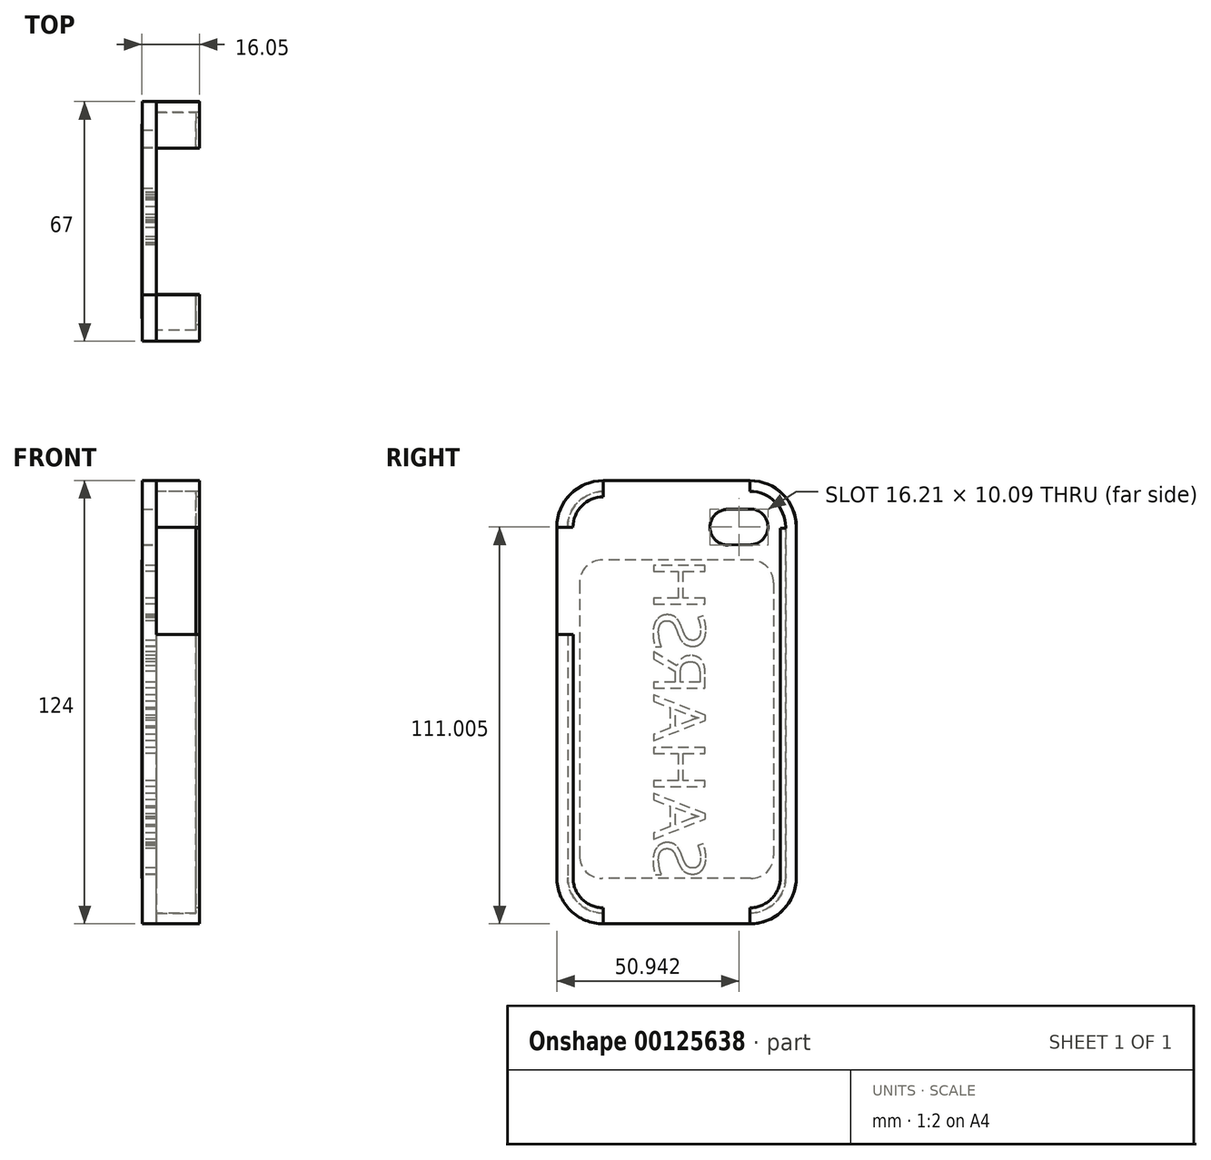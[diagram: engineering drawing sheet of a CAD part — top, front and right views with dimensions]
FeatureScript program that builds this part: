
annotation { "Feature Type Name" : "Feature", "Feature Type Description" : "" }
export const myFeature = defineFeature(function(context is Context, id is Id, definition is map)
    precondition{}
    {
        {
            var Q0;
            Q0=qCreatedBy(makeId("Right.planeOp"),FACE);
            var sketch = newSketch(context, id + "F0", { "sketchPlane" : qUnion([Q0])});
            skLineSegment(sketch, "E0.rect.bottom", {"start": v(20.5, 62) * mm, "end": v(-20.5, 62) * mm});
            skLineSegment(sketch, "E0.rect.top", {"start": v(20.5, -62) * mm, "end": v(-20.5, -62) * mm});
            skLineSegment(sketch, "E0.rect.left", {"start": v(33.5, 49) * mm, "end": v(33.5, -49) * mm});
            skLineSegment(sketch, "E0.rect.right", {"start": v(-33.5, 49) * mm, "end": v(-33.5, -49) * mm});
            skPoint(sketch, "E0.rect.middle", {"position": v(0, 0) * mm});
            skPoint(sketch, "E1.visualSharp", {"position": v(-33.5, 62) * mm});
            skArc(sketch, "E1.filletArc", {"start": v(-20.5, 62) * mm, "mid": v(-29.7, 58.2) * mm, "end": v(-33.5, 49) * mm});
            skPoint(sketch, "E2.visualSharp", {"position": v(-33.5, -62) * mm});
            skArc(sketch, "E2.filletArc", {"start": v(-33.5, -49) * mm, "mid": v(-29.7, -58.2) * mm, "end": v(-20.5, -62) * mm});
            skPoint(sketch, "E3.visualSharp", {"position": v(33.5, 62) * mm});
            skArc(sketch, "E3.filletArc", {"start": v(33.5, 49) * mm, "mid": v(29.7, 58.2) * mm, "end": v(20.5, 62) * mm});
            skPoint(sketch, "E4.visualSharp", {"position": v(33.5, -62) * mm});
            skArc(sketch, "E4.filletArc", {"start": v(20.5, -62) * mm, "mid": v(29.7, -58.2) * mm, "end": v(33.5, -49) * mm});
            skSolve(sketch);
        }
        {
            var Q0;
            Q0=qSketchRegion(id+"F0",true);
            extrude(context, id + "F1", {"entities" : qUnion([Q0]), "depth" : 4 * mm});
        }
        {
            var Q0;
            Q0=qCreatedBy(makeId("Right.planeOp"),FACE);
            var sketch = newSketch(context, id + "F2", { "sketchPlane" : qUnion([Q0])});
            skArc(sketch, "E5", {"start": v(20.7, 44.05) * mm, "mid": v(25.55, 49.12) * mm, "end": v(20.55, 54.05) * mm});
            skLineSegment(sketch, "E6", {"start": v(20.55, 54.05) * mm, "end": v(14.26, 53.96) * mm});
            skLineSegment(sketch, "E7", {"start": v(20.7, 44.05) * mm, "end": v(14.4, 43.96) * mm});
            skArc(sketch, "E8", {"start": v(14.26, 53.96) * mm, "mid": v(9.34, 48.89) * mm, "end": v(14.4, 43.96) * mm});
            skLineSegment(sketch, "E9", {"start": v(14.26, 53.96) * mm, "end": v(14.4, 43.96) * mm, "construction": true});
            skLineSegment(sketch, "E10", {"start": v(20.55, 54.05) * mm, "end": v(20.7, 44.05) * mm, "construction": true});
            skSolve(sketch);
        }
        {
            var Q0;
            Q0=makeQuery(id+"F2.imprint","IMPRINT",FACE,{"disambiguationData":[TD([[makeQuery(id+"F2.imprint","IMPRINT",EDGE,{"derivedFrom":sQuery(id+"F2.wireOp",EDGE,"E5")}),1.0]])]});
            extrude(context, id + "F3", {"entities" : qUnion([Q0]), "operationType" : NewBodyOperationType.REMOVE, "oppositeDirection" : true, "depth" : 25.4 * mm, "hasSecondDirection" : true, "secondDirectionOppositeDirection" : false, "secondDirectionDepth" : 33.72 * mm});
        }
        {
            var Q0;
            Q0=qCreatedBy(makeId("Right.planeOp"),FACE);
            var sketch = newSketch(context, id + "F4", { "sketchPlane" : qUnion([Q0])});
            skLineSegment(sketch, "E11", {"start": v(-30.46, 18.92) * mm, "end": v(-33.5, 18.92) * mm});
            skLineSegment(sketch, "E12", {"start": v(-33.5, 18.92) * mm, "end": v(-33.5, -49) * mm});
            skLineSegment(sketch, "E13", {"start": v(-33.5, -49) * mm, "end": v(-30.46, -49) * mm});
            skLineSegment(sketch, "E14", {"start": v(-30.46, -49) * mm, "end": v(-30.46, 18.92) * mm});
            skSolve(sketch);
        }
        {
            var Q0;
            Q0=qSketchRegion(id+"F4",true);
            extrude(context, id + "F5", {"entities" : qUnion([Q0]), "operationType" : NewBodyOperationType.ADD, "depth" : 16 * mm});
        }
        {
            var Q0;
            Q0=qCreatedBy(makeId("Right.planeOp"),FACE);
            var sketch = newSketch(context, id + "F6", { "sketchPlane" : qUnion([Q0])});
            skLineSegment(sketch, "E15", {"start": v(-33.5, -49) * mm, "end": v(-30.46, -49) * mm});
            skLineSegment(sketch, "E16", {"start": v(-20.5, -59) * mm, "end": v(-20.5, -62) * mm});
            skArc(sketch, "E17", {"start": v(-30.46, -49) * mm, "mid": v(-27.56, -56.07) * mm, "end": v(-20.5, -59) * mm});
            skArc(sketch, "E18", {"start": v(-33.5, -49) * mm, "mid": v(-29.7, -58.2) * mm, "end": v(-20.5, -62) * mm});
            skSolve(sketch);
        }
        {
            var Q0;
            Q0=qSketchRegion(id+"F6",true);
            extrude(context, id + "F7", {"entities" : qUnion([Q0]), "operationType" : NewBodyOperationType.ADD, "depth" : 16 * mm});
        }
        {
            var Q0;
            Q0=qCreatedBy(makeId("Right.planeOp"),FACE);
            var sketch = newSketch(context, id + "F8", { "sketchPlane" : qUnion([Q0])});
            skLineSegment(sketch, "E19", {"start": v(-30.47, 48.93) * mm, "end": v(-33.5, 48.93) * mm});
            skLineSegment(sketch, "E20", {"start": v(-20.5, 62) * mm, "end": v(-20.5, 58.97) * mm});
            skArc(sketch, "E21", {"start": v(-20.5, 58.97) * mm, "mid": v(-27.55, 56) * mm, "end": v(-30.47, 48.93) * mm});
            skArc(sketch, "E22", {"start": v(-20.5, 62) * mm, "mid": v(-29.7, 58.15) * mm, "end": v(-33.5, 48.93) * mm});
            skSolve(sketch);
        }
        {
            var Q0;
            Q0=qSketchRegion(id+"F8",true);
            extrude(context, id + "F9", {"entities" : qUnion([Q0]), "operationType" : NewBodyOperationType.ADD, "depth" : 16 * mm});
        }
        {
            var Q0;
            Q0=qCreatedBy(makeId("Right.planeOp"),FACE);
            var sketch = newSketch(context, id + "F10", { "sketchPlane" : qUnion([Q0])});
            skLineSegment(sketch, "E23", {"start": v(20.49, -62) * mm, "end": v(20.49, -59) * mm});
            skLineSegment(sketch, "E24", {"start": v(33.5, -49) * mm, "end": v(30.5, -49) * mm});
            skArc(sketch, "E25", {"start": v(20.49, -59) * mm, "mid": v(27.55, -56.06) * mm, "end": v(30.5, -49) * mm});
            skArc(sketch, "E26", {"start": v(20.49, -62) * mm, "mid": v(29.67, -58.19) * mm, "end": v(33.5, -49) * mm});
            skSolve(sketch);
        }
        {
            var Q0;
            Q0=qSketchRegion(id+"F10",true);
            extrude(context, id + "F11", {"entities" : qUnion([Q0]), "operationType" : NewBodyOperationType.ADD, "depth" : 16 * mm});
        }
        {
            var Q0;
            Q0=qCreatedBy(makeId("Right.planeOp"),FACE);
            var sketch = newSketch(context, id + "F12", { "sketchPlane" : qUnion([Q0])});
            skLineSegment(sketch, "E27", {"start": v(33.46, 49) * mm, "end": v(30.5, 49) * mm});
            skLineSegment(sketch, "E28", {"start": v(20.5, 62) * mm, "end": v(20.5, 58.99) * mm});
            skArc(sketch, "E29", {"start": v(33.46, 49) * mm, "mid": v(29.66, 58.17) * mm, "end": v(20.5, 62) * mm});
            skArc(sketch, "E30", {"start": v(30.5, 49) * mm, "mid": v(27.55, 56.05) * mm, "end": v(20.5, 58.99) * mm});
            skSolve(sketch);
        }
        {
            var Q0;
            Q0=qSketchRegion(id+"F12",true);
            extrude(context, id + "F13", {"entities" : qUnion([Q0]), "operationType" : NewBodyOperationType.ADD, "depth" : 16 * mm});
        }
        {
            var Q0;
            Q0=qCreatedBy(makeId("Right.planeOp"),FACE);
            var sketch = newSketch(context, id + "F14", { "sketchPlane" : qUnion([Q0])});
            skLineSegment(sketch, "E31", {"start": v(30.5, -49) * mm, "end": v(33.49, -49) * mm});
            skLineSegment(sketch, "E32", {"start": v(33.49, -49) * mm, "end": v(33.49, 49) * mm});
            skLineSegment(sketch, "E33", {"start": v(33.49, 49) * mm, "end": v(30.5, 49) * mm});
            skLineSegment(sketch, "E34", {"start": v(30.5, 49) * mm, "end": v(30.5, -49) * mm});
            skSolve(sketch);
        }
        {
            var Q0;
            Q0=qSketchRegion(id+"F14",true);
            extrude(context, id + "F15", {"entities" : qUnion([Q0]), "operationType" : NewBodyOperationType.ADD, "depth" : 16 * mm});
        }
        {
            var Q0;
            Q0=qCreatedBy(makeId("Right.planeOp"),FACE);
            var sketch = newSketch(context, id + "F16", { "sketchPlane" : qUnion([Q0])});
            skLineSegment(sketch, "E35", {"start": v(-30.46, 18.92) * mm, "end": v(-30.46, -49.07) * mm});
            skLineSegment(sketch, "E36", {"start": v(-30.46, -49.07) * mm, "end": v(-28.96, -49.07) * mm});
            skLineSegment(sketch, "E37", {"start": v(-28.96, -49.07) * mm, "end": v(-28.96, 18.92) * mm});
            skLineSegment(sketch, "E38", {"start": v(-28.96, 18.92) * mm, "end": v(-30.46, 18.92) * mm});
            skLineSegment(sketch, "E39", {"start": v(-20.5, -59) * mm, "end": v(-20.5, -57.5) * mm});
            skArc(sketch, "E40", {"start": v(-30.46, -49.07) * mm, "mid": v(-27.53, -56.1) * mm, "end": v(-20.5, -59) * mm});
            skArc(sketch, "E41", {"start": v(-28.96, -49.07) * mm, "mid": v(-26.47, -55.04) * mm, "end": v(-20.5, -57.5) * mm});
            skLineSegment(sketch, "E42", {"start": v(-30.47, 48.93) * mm, "end": v(-28.97, 48.93) * mm});
            skLineSegment(sketch, "E43", {"start": v(-20.5, 58.97) * mm, "end": v(-20.5, 57.47) * mm});
            skArc(sketch, "E44", {"start": v(-20.5, 58.97) * mm, "mid": v(-27.55, 56) * mm, "end": v(-30.47, 48.93) * mm});
            skArc(sketch, "E45", {"start": v(-20.5, 57.47) * mm, "mid": v(-26.5, 54.95) * mm, "end": v(-28.97, 48.93) * mm});
            skLineSegment(sketch, "E46", {"start": v(30.5, 48.62) * mm, "end": v(29, 48.62) * mm});
            skLineSegment(sketch, "E47", {"start": v(30.5, -49) * mm, "end": v(29, -49) * mm});
            skLineSegment(sketch, "E48", {"start": v(29, -49) * mm, "end": v(29, 48.62) * mm});
            skLineSegment(sketch, "E49", {"start": v(30.5, 48.62) * mm, "end": v(30.5, -49) * mm});
            skLineSegment(sketch, "E50", {"start": v(20.49, -59) * mm, "end": v(20.49, -57.5) * mm});
            skArc(sketch, "E51", {"start": v(20.49, -59) * mm, "mid": v(27.54, -56.06) * mm, "end": v(30.5, -49) * mm});
            skArc(sketch, "E52", {"start": v(20.49, -57.5) * mm, "mid": v(26.5, -55.02) * mm, "end": v(29, -49) * mm});
            skSolve(sketch);
        }
        {
            var Q0;
            Q0=qSketchRegion(id+"F16",true);
            extrude(context, id + "F17", {"entities" : qUnion([Q0]), "operationType" : NewBodyOperationType.ADD, "depth" : 16 * mm, "hasSecondDirection" : true, "secondDirectionOppositeDirection" : false, "secondDirectionDepth" : 15 * mm});
        }
        {
            var Q0;
            Q0=makeQuery(id+"F7.boolean.opBoolean","MERGE",FACE,{"derivedFrom":[makeQuery(id+"F1.opExtrude","CAP_FACE",FACE,{"disambiguationData":[OSD([sQuery(id+"F0.wireOp",EDGE,"E0.rect.bottom"),sQuery(id+"F0.wireOp",EDGE,"E0.rect.top"),sQuery(id+"F0.wireOp",EDGE,"E0.rect.left"),sQuery(id+"F0.wireOp",EDGE,"E0.rect.right"),sQuery(id+"F0.wireOp",EDGE,"E1.filletArc"),sQuery(id+"F0.wireOp",EDGE,"E2.filletArc"),sQuery(id+"F0.wireOp",EDGE,"E3.filletArc"),sQuery(id+"F0.wireOp",EDGE,"E4.filletArc")])],"isStart":true}),makeQuery(id+"F7.opExtrude","CAP_FACE",FACE,{"disambiguationData":[OSD([sQuery(id+"F6.wireOp",EDGE,"E15"),sQuery(id+"F6.wireOp",EDGE,"E16"),sQuery(id+"F6.wireOp",EDGE,"E17"),sQuery(id+"F6.wireOp",EDGE,"E18")])],"isStart":true})]});
            var sketch = newSketch(context, id + "F18", { "sketchPlane" : qUnion([Q0])});
            skLineSegment(sketch, "E53.bottom", {"start": v(-20.8, 39.78) * mm, "end": v(20.8, 39.78) * mm});
            skLineSegment(sketch, "E53.top", {"start": v(-20.8, -49.3) * mm, "end": v(20.8, -49.3) * mm});
            skLineSegment(sketch, "E53.left", {"start": v(-27.15, 33.43) * mm, "end": v(-27.15, -42.95) * mm});
            skLineSegment(sketch, "E53.right", {"start": v(27.15, 33.42) * mm, "end": v(27.15, -42.95) * mm});
            skPoint(sketch, "E54.visualSharp", {"position": v(-27.15, 39.78) * mm});
            skArc(sketch, "E54.filletArc", {"start": v(-20.8, 39.78) * mm, "mid": v(-25.3, 37.92) * mm, "end": v(-27.15, 33.43) * mm});
            skPoint(sketch, "E55.visualSharp", {"position": v(-27.15, -49.3) * mm});
            skArc(sketch, "E55.filletArc", {"start": v(-27.15, -42.95) * mm, "mid": v(-25.3, -47.44) * mm, "end": v(-20.8, -49.3) * mm});
            skPoint(sketch, "E56.visualSharp", {"position": v(27.15, -49.3) * mm});
            skArc(sketch, "E56.filletArc", {"start": v(20.8, -49.3) * mm, "mid": v(25.3, -47.44) * mm, "end": v(27.15, -42.95) * mm});
            skPoint(sketch, "E57.visualSharp", {"position": v(27.15, 39.78) * mm});
            skArc(sketch, "E57.filletArc", {"start": v(27.15, 33.42) * mm, "mid": v(25.3, 37.92) * mm, "end": v(20.8, 39.78) * mm});
            skSolve(sketch);
        }
        {
            var Q0;
            Q0 = qSketchRegion(id + "F18", true);
            extrude(context, id + "F19", {"entities" : qUnion([Q0]), "operationType" : NewBodyOperationType.ADD, "depth" : 0.05 * mm});
        }
        {
            var Q0;
            Q0=makeQuery(id+"F19.opExtrude","CAP_FACE",FACE,{"disambiguationData":[OSD([sQuery(id+"F18.wireOp",EDGE,"E53.bottom"),sQuery(id+"F18.wireOp",EDGE,"E53.top"),sQuery(id+"F18.wireOp",EDGE,"E53.left"),sQuery(id+"F18.wireOp",EDGE,"E53.right"),sQuery(id+"F18.wireOp",EDGE,"E54.filletArc"),sQuery(id+"F18.wireOp",EDGE,"E55.filletArc"),sQuery(id+"F18.wireOp",EDGE,"E56.filletArc"),sQuery(id+"F18.wireOp",EDGE,"E57.filletArc")])],"isStart":false});
            var sketch = newSketch(context, id + "F20", { "sketchPlane" : qUnion([Q0])});
            skText(sketch, "E58", { "text": "SAHARSH", "fontName": "OpenSans-Regular.ttf"});
            const initialGuessF20  = {"E58": [0.00637, -0.0493, 0, 1, 0.01447]};
            skSetInitialGuess(sketch, initialGuessF20);
            skSolve(sketch);
        }
        {
            var Q0;
            Q0 = qSketchRegion(id + "F20", true);
            extrude(context, id + "F21", {"entities" : qUnion([Q0]), "operationType" : NewBodyOperationType.REMOVE, "oppositeDirection" : true, "depth" : 4 * mm});
        }
    });
